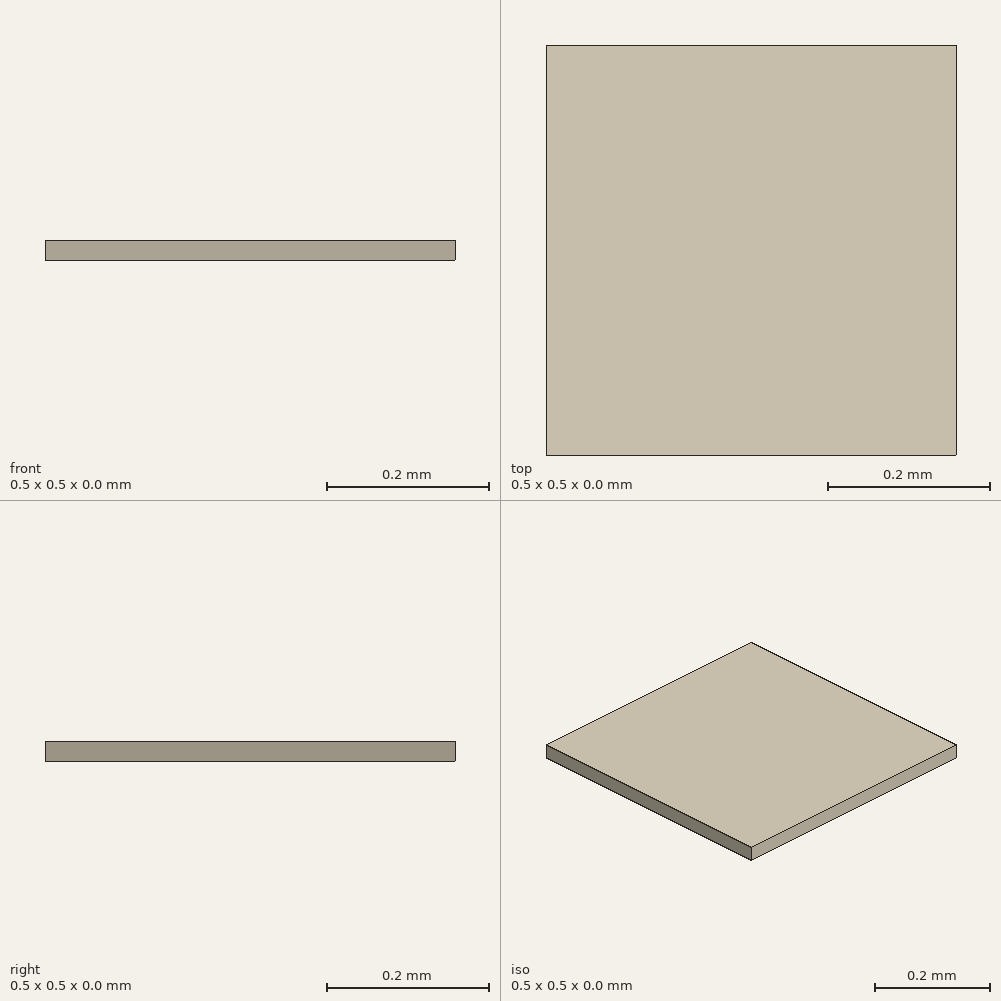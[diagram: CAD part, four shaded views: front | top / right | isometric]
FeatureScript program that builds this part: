
annotation { "Feature Type Name" : "Feature", "Feature Type Description" : "" }
export const myFeature = defineFeature(function(context is Context, id is Id, definition is map)
    precondition{}
    {
        {
            var Q0;
            Q0=qCreatedBy(makeId("Top.planeOp"),FACE);
            var sketch = newSketch(context, id + "F0", { "sketchPlane" : qUnion([Q0])});
            skLineSegment(sketch, "E0.bottom", {"start": v(0, 0) * mm, "end": v(0.5, 0) * mm});
            skLineSegment(sketch, "E0.top", {"start": v(0, 0.5) * mm, "end": v(0.5, 0.5) * mm});
            skLineSegment(sketch, "E0.left", {"start": v(0, 0) * mm, "end": v(0, 0.5) * mm});
            skLineSegment(sketch, "E0.right", {"start": v(0.5, 0) * mm, "end": v(0.5, 0.5) * mm});
            skSolve(sketch);
        }
        {
            var Q0;
            Q0 = qSketchRegion(id + "F0", true);
            extrude(context, id + "F1", {"entities" : qUnion([Q0]), "depth" : 0.03 * mm, "offsetDistance" : 25.4 * mm});
        }
    });
